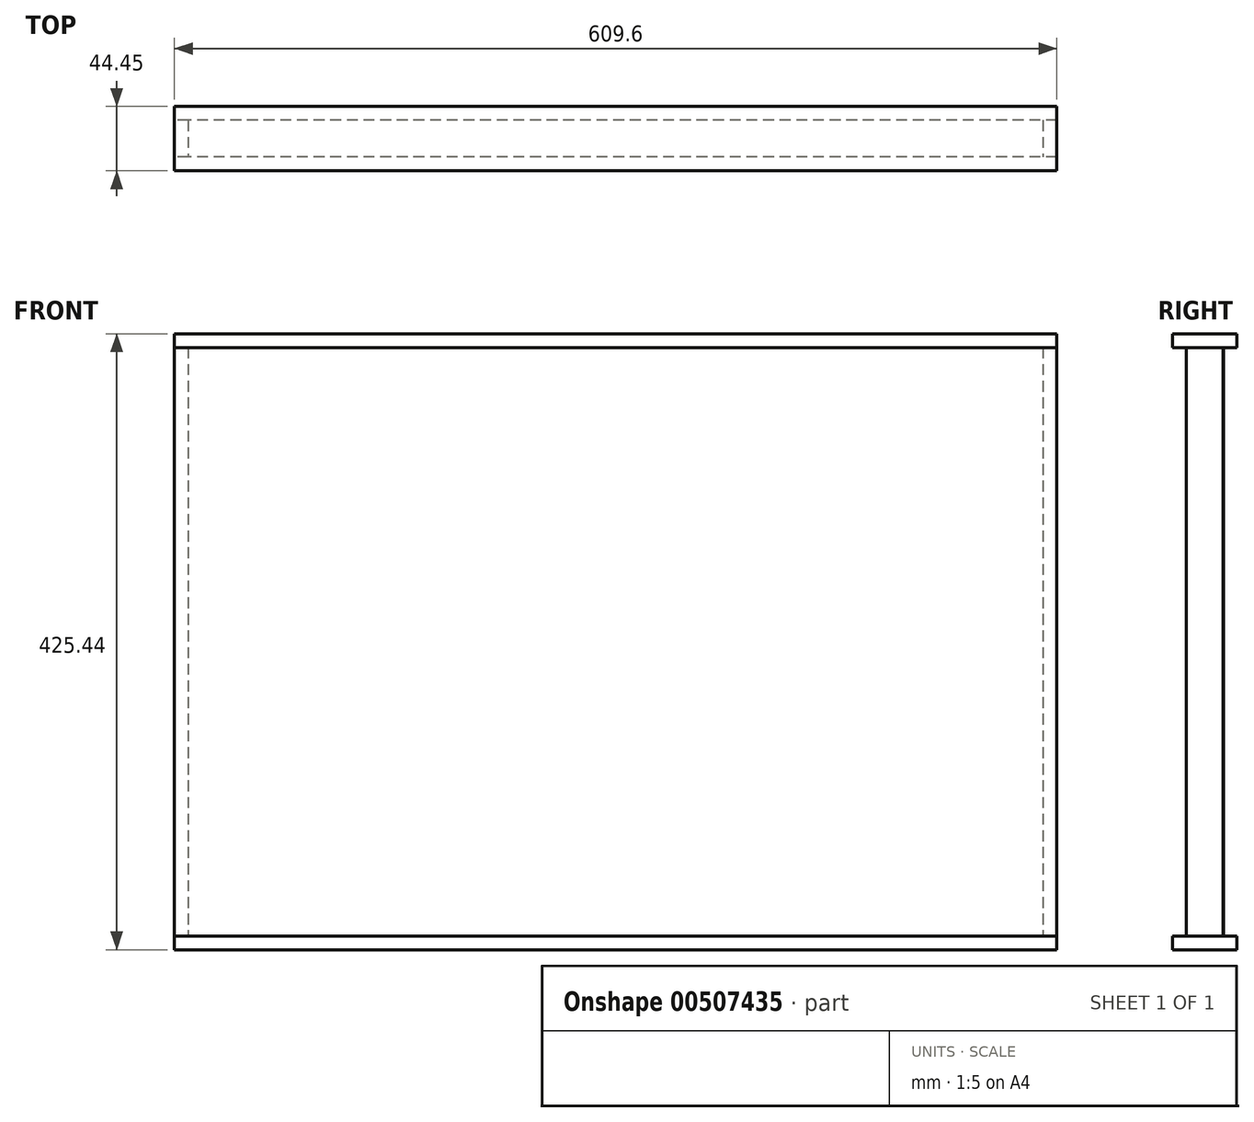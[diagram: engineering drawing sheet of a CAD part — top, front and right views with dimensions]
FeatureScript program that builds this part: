
annotation { "Feature Type Name" : "Feature", "Feature Type Description" : "" }
export const myFeature = defineFeature(function(context is Context, id is Id, definition is map)
    precondition{}
    {
        {
            var Q0;
            Q0=qCreatedBy(makeId("Front.planeOp"),FACE);
            var sketch = newSketch(context, id + "F0", { "sketchPlane" : qUnion([Q0])});
            skLineSegment(sketch, "E0.bottom", {"start": v(304.8, 203.2) * mm, "end": v(-304.8, 203.2) * mm});
            skLineSegment(sketch, "E0.top", {"start": v(304.8, -203.2) * mm, "end": v(-304.8, -203.2) * mm});
            skLineSegment(sketch, "E0.left", {"start": v(304.8, 203.2) * mm, "end": v(304.8, -203.2) * mm});
            skLineSegment(sketch, "E0.right", {"start": v(-304.8, 203.2) * mm, "end": v(-304.8, -203.2) * mm});
            skPoint(sketch, "E0.middle", {"position": v(0, 0) * mm});
            skSolve(sketch);
        }
        {
            var Q0;
            Q0=makeQuery(id+"F0.imprint","IMPRINT",FACE,{"disambiguationData":[TD([[makeQuery(id+"F0.imprint","IMPRINT",EDGE,{"derivedFrom":sQuery(id+"F0.wireOp",EDGE,"E0.bottom")}),1.0]])]});
            extrude(context, id + "F1", {"entities" : qUnion([Q0]), "depth" : 3 / 203.2 * mm});
        }
        {
            var Q0;
            Q0=makeQuery(id+"F1.opExtrude","CAP_FACE",FACE,{"disambiguationData":[OSD([sQuery(id+"F0.wireOp",EDGE,"E0.bottom"),sQuery(id+"F0.wireOp",EDGE,"E0.top"),sQuery(id+"F0.wireOp",EDGE,"E0.left"),sQuery(id+"F0.wireOp",EDGE,"E0.right")])],"isStart":true});
            var sketch = newSketch(context, id + "F2", { "sketchPlane" : qUnion([Q0])});
            skLineSegment(sketch, "E1.bottom", {"start": v(-304.8, 203.2) * mm, "end": v(-295.27, 203.2) * mm});
            skLineSegment(sketch, "E1.top", {"start": v(-304.8, -203.2) * mm, "end": v(-295.27, -203.2) * mm});
            skLineSegment(sketch, "E1.left", {"start": v(-304.8, 203.2) * mm, "end": v(-304.8, -203.2) * mm});
            skLineSegment(sketch, "E1.right", {"start": v(-295.27, 203.2) * mm, "end": v(-295.27, -203.2) * mm});
            skLineSegment(sketch, "E2.bottom", {"start": v(304.8, 203.2) * mm, "end": v(295.27, 203.2) * mm});
            skLineSegment(sketch, "E2.top", {"start": v(304.8, -203.2) * mm, "end": v(295.28, -203.2) * mm});
            skLineSegment(sketch, "E2.left", {"start": v(304.8, 203.2) * mm, "end": v(304.8, -203.2) * mm});
            skLineSegment(sketch, "E2.right", {"start": v(295.27, 203.2) * mm, "end": v(295.28, -203.2) * mm});
            skSolve(sketch);
        }
        {
            var Q0;
            Q0 = qSketchRegion(id + "F2", true);
            extrude(context, id + "F3", {"entities" : qUnion([Q0]), "depth" : 25.4 * mm});
        }
        {
            var Q0;
            Q0=makeQuery(id+"F3.opExtrude","CAP_FACE",FACE,{"disambiguationData":[OSD([sQuery(id+"F2.wireOp",EDGE,"E1.bottom"),sQuery(id+"F2.wireOp",EDGE,"E1.top"),sQuery(id+"F2.wireOp",EDGE,"E1.left"),sQuery(id+"F2.wireOp",EDGE,"E1.right")])],"isStart":false});
            var sketch = newSketch(context, id + "F4", { "sketchPlane" : qUnion([Q0])});
            skLineSegment(sketch, "E3.bottom", {"start": v(-304.8, -203.2) * mm, "end": v(304.8, -203.2) * mm});
            skLineSegment(sketch, "E3.top", {"start": v(-304.8, 203.2) * mm, "end": v(304.8, 203.2) * mm});
            skLineSegment(sketch, "E3.left", {"start": v(-304.8, -203.2) * mm, "end": v(-304.8, 203.2) * mm});
            skLineSegment(sketch, "E3.right", {"start": v(304.8, -203.2) * mm, "end": v(304.8, 203.2) * mm});
            skSolve(sketch);
        }
        {
            var Q0;
            {var subQ2=sQuery(id+"F4.wireOp",EDGE,"E3.right");Q0=makeQuery(id+"F4.imprint","IMPRINT",FACE,{"disambiguationData":[TD([[makeQuery(id+"F4.imprint","IMPRINT",EDGE,{"derivedFrom":subQ2}),1.0]])]});}
            var Q1;
            {var subQ0=sQuery(id+"F4.wireOp",EDGE,"E3.left");Q1=makeQuery(id+"F4.imprint","IMPRINT",FACE,{"disambiguationData":[TD([[makeQuery(id+"F4.imprint","IMPRINT",EDGE,{"derivedFrom":subQ0}),1.0]])]});}
            extrude(context, id + "F5", {"entities" : qUnion([Q0, Q1]), "depth" : 3 / 203.2 * mm});
        }
        {
            var Q0;
            Q0=makeQuery(id+"F1.opExtrude","SWEPT_FACE",FACE,{"disambiguationData":[OSD([sQuery(id+"F0.wireOp",EDGE,"E0.top")])]});
            var sketch = newSketch(context, id + "F6", { "sketchPlane" : qUnion([Q0])});
            skLineSegment(sketch, "E4.bottom", {"start": v(-304.8, 9.53) * mm, "end": v(304.8, 9.53) * mm});
            skLineSegment(sketch, "E4.top", {"start": v(-304.8, -34.93) * mm, "end": v(304.8, -34.93) * mm});
            skLineSegment(sketch, "E4.left", {"start": v(-304.8, 9.53) * mm, "end": v(-304.8, -34.93) * mm});
            skLineSegment(sketch, "E4.right", {"start": v(304.8, 9.52) * mm, "end": v(304.8, -34.93) * mm});
            skSolve(sketch);
        }
        {
            var Q0;
            Q0 = qSketchRegion(id + "F6", true);
            extrude(context, id + "F7", {"entities" : qUnion([Q0]), "depth" : 9.52 * mm});
        }
        {
            var Q0;
            Q0=makeQuery(id+"F5.opExtrude","SWEPT_FACE",FACE,{"disambiguationData":[OSD([sQuery(id+"F4.wireOp",EDGE,"E3.top")])]});
            var sketch = newSketch(context, id + "F8", { "sketchPlane" : qUnion([Q0])});
            skLineSegment(sketch, "E5.bottom", {"start": v(-304.8, 34.93) * mm, "end": v(304.8, 34.93) * mm});
            skLineSegment(sketch, "E5.top", {"start": v(-304.8, -9.53) * mm, "end": v(304.8, -9.53) * mm});
            skLineSegment(sketch, "E5.left", {"start": v(-304.8, 34.93) * mm, "end": v(-304.8, -9.53) * mm});
            skLineSegment(sketch, "E5.right", {"start": v(304.8, 34.93) * mm, "end": v(304.8, -9.53) * mm});
            skSolve(sketch);
        }
        {
            var Q0;
            Q0 = qSketchRegion(id + "F8", true);
            extrude(context, id + "F9", {"entities" : qUnion([Q0]), "depth" : 9.52 * mm});
        }
    });
